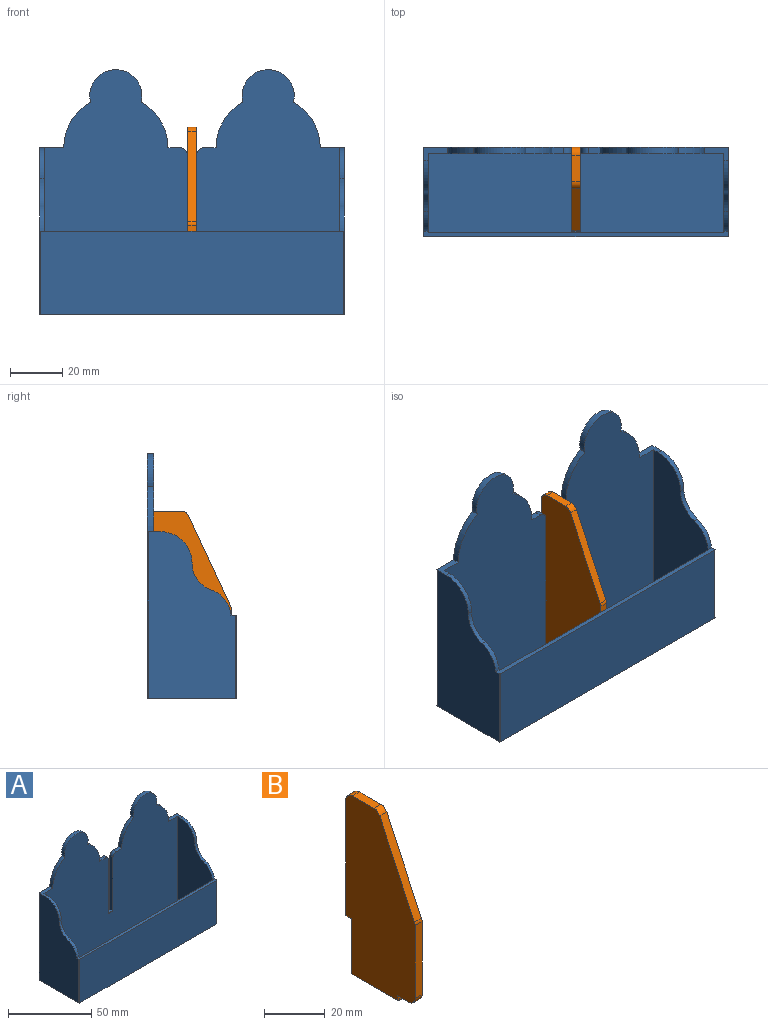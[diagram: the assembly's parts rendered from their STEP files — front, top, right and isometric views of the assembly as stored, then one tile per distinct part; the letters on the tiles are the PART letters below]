
ASSEMBLY  parts=2 mates=1
PART A: 41 faces, bbox 117.1x34.4x94 mm
  f0: plane 4.5x2.5mm, normal (0,0,1), area 11.2mm2, adj f3,f4,f30,f33
  f1: plane 9.3x5.2mm, normal (0,0,1), area 28.1mm2, adj f3,f4,f5,f10,f24,f31,f36
  f2: plane 4.5x2.5mm, normal (0,0,1), area 11.2mm2, adj f3,f4,f27,f34
  f3: plane 116.3x94mm, normal (0,1,0), area 8896.3mm2, adj f0,f1,f2,f11,f12,f17,f18,f26
  f4: plane 113.5x94mm, normal (0,-1,0), area 8517.7mm2, adj f0,f1,f2,f8,f10,f11,f12,f13
  f5: plane 64x33.6mm, normal (-1,0,0), area 1725.5mm2, adj f1,f17,f19,f20,f22,f24,f36,f37
  f6: plane 116.3x32mm, normal (0,-1,0), area 3721.6mm2, adj f17,f19,f37,f38
  f7: plane 64x33.6mm, normal (1,0,0), area 1725.5mm2, adj f17,f19,f21,f23,f25,f26,f38,f39
  f8: plane 62.2x30.1mm, normal (-1,0,0), area 1492.1mm2, adj f4,f9,f13,f19,f21,f23,f25,f26
  f9: plane 113.5x30.2mm, normal (0,1,0), area 3427.7mm2, adj f8,f10,f13,f19
  f10: plane 62.2x30.1mm, normal (1,0,0), area 1492.1mm2, adj f1,f4,f9,f13,f19,f20,f22,f24
  f11: plane 39.5x2.5mm, normal (1,0,0), area 97.8mm2, adj f3,f4,f18,f33,f35
  f12: plane 39.5x2.5mm, normal (-1,0,0), area 97.8mm2, adj f3,f4,f18,f34,f35
  f13: plane 113.5x30.1mm, normal (0,0,1), area 3336.2mm2, adj f4,f8,f9,f10,f14,f16,f40
  f14: plane 22.9x1.8mm, normal (-1,0,0), area 40.5mm2, adj f4,f13,f15,f17,f40
  f15: plane 3.5x1.4mm, normal (0,1,0), area 4.9mm2, adj f14,f16,f17,f40
  f16: plane 22.9x1.8mm, normal (1,0,0), area 40.5mm2, adj f4,f13,f15,f17,f40
  f17: plane 117.1x34.4mm, normal (0,0,-1), area 3949.4mm2, adj f3,f4,f5,f6,f7,f14,f15,f16
  f18: plane 3.5x2.1mm, normal (0,0,1), area 7.3mm2, adj f3,f11,f12,f35
  f19: plane 117.1x2.23mm, normal (0,0,1), area 212.3mm2, adj f5,f6,f7,f8,f9,f10,f20,f21
  f20: cylinder r=11mm len=9.57mm, axis (1,0,0), area 23.1mm2, adj f5,f10,f19,f22
  f21: cylinder r=11mm len=9.57mm, axis (1,0,0), area 23.1mm2, adj f7,f8,f19,f23
  f22: cylinder r=11mm len=10.43mm, axis (1,0,0), area 24.7mm2, adj f5,f10,f20,f24
  f23: cylinder r=11mm len=10.43mm, axis (1,0,0), area 24.7mm2, adj f7,f8,f21,f25
  f24: cylinder r=12mm len=12mm, axis (1,0,0), area 33.9mm2, adj f1,f5,f10,f22
  f25: cylinder r=12mm len=12mm, axis (1,0,0), area 33.9mm2, adj f7,f8,f23,f26
  f26: plane 9.3x5.2mm, normal (0,0,1), area 28.1mm2, adj f3,f4,f7,f8,f25,f28,f39
  f27: cylinder r=20mm len=17.5mm, axis (0,-1,0), area 53.3mm2, adj f2,f3,f4,f29
  f28: cylinder r=20mm len=17.5mm, axis (0,-1,0), area 53.3mm2, adj f3,f4,f26,f29
  f29: cylinder r=10mm len=20mm, axis (0,-1,0), area 91.2mm2, adj f3,f4,f27,f28
  f30: cylinder r=20mm len=17.5mm, axis (0,-1,0), area 53.3mm2, adj f0,f3,f4,f32
  f31: cylinder r=20mm len=17.5mm, axis (0,-1,0), area 53.3mm2, adj f1,f3,f4,f32
  f32: cylinder r=10mm len=20mm, axis (0,-1,0), area 91.2mm2, adj f3,f4,f30,f31
  f33: cylinder r=3mm len=3mm, axis (0,-1,0), area 11.8mm2, adj f0,f3,f4,f11
  f34: cylinder r=3mm len=3mm, axis (0,1,0), area 11.8mm2, adj f2,f3,f4,f12
  f35: cylinder r=0.4mm len=3.5mm, axis (1,0,0), area 2.2mm2, adj f4,f11,f12,f18
  f36: cylinder r=0.4mm len=64mm, axis (0,0,1), area 40.2mm2, adj f1,f3,f5,f17
  f37: cylinder r=0.4mm len=32mm, axis (0,0,1), area 20.1mm2, adj f5,f6,f17,f19
  f38: cylinder r=0.4mm len=32mm, axis (0,0,-1), area 20.1mm2, adj f6,f7,f17,f19
  f39: cylinder r=0.4mm len=64mm, axis (0,0,-1), area 40.2mm2, adj f3,f7,f17,f26
  f40: cylinder r=0.4mm len=3.5mm, axis (1,0,0), area 2.2mm2, adj f13,f14,f15,f16
PART B: 19 faces, bbox 3.3x32.2x71.9 mm
  f0: plane 47x3.25mm, normal (0,1,0), area 152.7mm2, adj f1,f12,f13,f14,f16,f18
  f1: cylinder r=3mm len=3.25mm, axis (-1,0,0), area 15.3mm2, adj f0,f2,f13,f14
  f2: plane 9.99x3.25mm, normal (0,0,1), area 32.5mm2, adj f1,f3,f13,f14
  f3: cylinder r=3mm len=3.25mm, axis (-1,0,0), area 11.1mm2, adj f2,f4,f13,f14
  f4: plane 34.67x16.16mm, normal (0,-0.91,0.42), area 124.3mm2, adj f3,f5,f13,f14
  f5: cylinder r=3mm len=3.25mm, axis (-1,0,0), area 4.3mm2, adj f4,f6,f13,f14
  f6: plane 29.34x3.25mm, normal (0,-1,0), area 95.3mm2, adj f5,f7,f13,f14
  f7: cylinder r=3mm len=3.25mm, axis (-1,0,0), area 15.3mm2, adj f6,f8,f13,f14
  f8: plane 5.15x3.25mm, normal (0,0,-1), area 15.5mm2, adj f7,f9,f13,f14,f15,f17
  f9: plane 2.45x1.9mm, normal (0,-1,0), area 4.7mm2, adj f8,f10,f15,f17
  f10: plane 22x3.25mm, normal (0,0,-1), area 71.4mm2, adj f9,f11,f13,f14,f15,f17
  f11: plane 22.3x3.25mm, normal (0,1,0), area 71.2mm2, adj f10,f12,f13,f14,f16,f18
  f12: plane 2.45x2.4mm, normal (0,0,-1), area 5.9mm2, adj f0,f11,f16,f18
  f13: plane 71.9x32.15mm, normal (1,0,0), area 1918.9mm2, adj f0,f1,f2,f3,f4,f5,f6,f7
  f14: plane 71.9x32.15mm, normal (-1,0,0), area 1918.9mm2, adj f0,f1,f2,f3,f4,f5,f6,f7
  f15: cylinder r=0.4mm len=1.9mm, axis (0,0,-1), area 1.2mm2, adj f8,f9,f10,f14
  f16: cylinder r=0.4mm len=2.4mm, axis (0,1,0), area 1.5mm2, adj f0,f11,f12,f14
  f17: cylinder r=0.4mm len=1.9mm, axis (0,0,1), area 1.2mm2, adj f8,f9,f10,f13
  f18: cylinder r=0.4mm len=2.4mm, axis (0,-1,0), area 1.5mm2, adj f0,f11,f12,f13
PLACE A t=(4.74,17.46,14.95)mm
PLACE B t=(4.74,17.46,16.85)mm
MATE fastened B.f11 <-> A.f4  axis (0,1,0) through (4.74,17.46,36.85)mm
